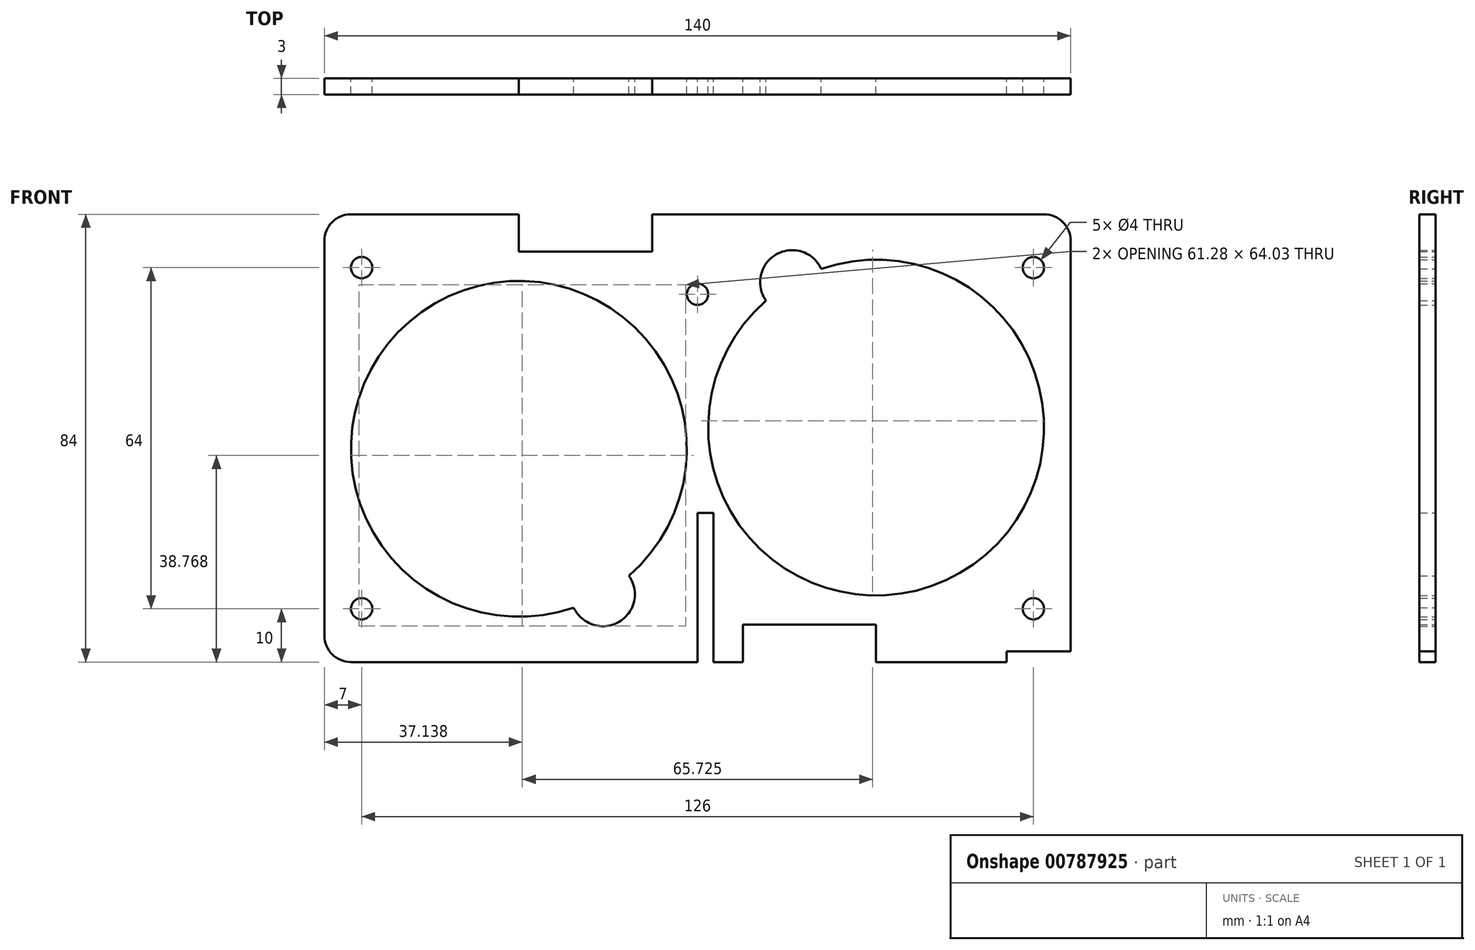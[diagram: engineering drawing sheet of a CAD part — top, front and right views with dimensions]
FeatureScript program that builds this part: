
annotation { "Feature Type Name" : "Feature", "Feature Type Description" : "" }
export const myFeature = defineFeature(function(context is Context, id is Id, definition is map)
    precondition{}
    {
        {
            var Q0;
            Q0=qCreatedBy(makeId("Front.planeOp"),FACE);
            var sketch = newSketch(context, id + "F0", { "sketchPlane" : qUnion([Q0])});
            skLineSegment(sketch, "E0.bottom", {"start": v(-65, -42) * mm, "end": v(0, -42) * mm});
            skLineSegment(sketch, "E0.top", {"start": v(-65, 42) * mm, "end": v(-33.5, 42) * mm});
            skLineSegment(sketch, "E0.left", {"start": v(-70, -37) * mm, "end": v(-70, 37) * mm});
            skLineSegment(sketch, "E0.right", {"start": v(70, -40) * mm, "end": v(70, 37) * mm});
            skPoint(sketch, "E0.middle", {"position": v(0, 0) * mm});
            skLineSegment(sketch, "E1", {"start": v(70, -40) * mm, "end": v(70, 2) * mm, "construction": true});
            skLineSegment(sketch, "E2", {"start": v(70, 2) * mm, "end": v(-70, 2) * mm, "construction": true});
            skLineSegment(sketch, "E3", {"start": v(-70, -42) * mm, "end": v(-70, -2) * mm, "construction": true});
            skLineSegment(sketch, "E4", {"start": v(-70, -2) * mm, "end": v(70, -2) * mm, "construction": true});
            skLineSegment(sketch, "E5", {"start": v(-70, -42) * mm, "end": v(0, -42) * mm, "construction": true});
            skLineSegment(sketch, "E6", {"start": v(0, -42) * mm, "end": v(0, 42) * mm, "construction": true});
            skLineSegment(sketch, "E7", {"start": v(0, -42) * mm, "end": v(0, 2) * mm, "construction": true});
            skLineSegment(sketch, "E8", {"start": v(0, -42) * mm, "end": v(0, -14) * mm});
            skLineSegment(sketch, "E9", {"start": v(0, -14) * mm, "end": v(0, -14) * mm});
            skLineSegment(sketch, "E10", {"start": v(-70, -42) * mm, "end": v(-33.5, -42) * mm, "construction": true});
            skLineSegment(sketch, "E11", {"start": v(-33.5, -42) * mm, "end": v(-33.5, 42) * mm, "construction": true});
            skPoint(sketch, "E12", {"position": v(-33.5, -2) * mm});
            skPoint(sketch, "E13", {"position": v(-33.5, 2) * mm});
            skArc(sketch, "E14", {"start": v(-12.86, -25.8) * mm, "mid": v(-49.25, 25.28) * mm, "end": v(-23.2, -31.77) * mm});
            skLineSegment(sketch, "E15", {"start": v(58, -42) * mm, "end": v(33.5, -42) * mm, "construction": true});
            skLineSegment(sketch, "E16", {"start": v(33.5, -42) * mm, "end": v(33.5, 42) * mm, "construction": true});
            skPoint(sketch, "E17", {"position": v(33.5, -2) * mm});
            skPoint(sketch, "E18", {"position": v(33.5, 2) * mm});
            skArc(sketch, "E19", {"start": v(12.86, 25.8) * mm, "mid": v(49.25, -25.28) * mm, "end": v(23.2, 31.77) * mm});
            skLineSegment(sketch, "E20", {"start": v(-33.5, -2) * mm, "end": v(-17.75, -29.28) * mm, "construction": true});
            skArc(sketch, "E21", {"start": v(-23.2, -31.77) * mm, "mid": v(-14.75, -34.48) * mm, "end": v(-12.86, -25.8) * mm});
            skLineSegment(sketch, "E22", {"start": v(-70, 42) * mm, "end": v(-63, 42) * mm, "construction": true});
            skLineSegment(sketch, "E23", {"start": v(-63, 42) * mm, "end": v(-63, -42) * mm, "construction": true});
            skLineSegment(sketch, "E24", {"start": v(-70, 42) * mm, "end": v(-70, 32) * mm, "construction": true});
            skLineSegment(sketch, "E25", {"start": v(-70, 32) * mm, "end": v(-63, 32) * mm, "construction": true});
            skLineSegment(sketch, "E26", {"start": v(-70, -42) * mm, "end": v(-70, -32) * mm, "construction": true});
            skLineSegment(sketch, "E27", {"start": v(-70, -32) * mm, "end": v(-63, -32) * mm, "construction": true});
            skCircle(sketch, "E28", {"center": v(-63, -32) * mm, "radius": 2 * mm});
            skLineSegment(sketch, "E29", {"start": v(70, 42) * mm, "end": v(63, 42) * mm, "construction": true});
            skLineSegment(sketch, "E30", {"start": v(63, 42) * mm, "end": v(63, -40) * mm, "construction": true});
            skLineSegment(sketch, "E31", {"start": v(70, 42) * mm, "end": v(70, 32) * mm, "construction": true});
            skLineSegment(sketch, "E32", {"start": v(70, 32) * mm, "end": v(63, 32) * mm, "construction": true});
            skLineSegment(sketch, "E33", {"start": v(70, -40) * mm, "end": v(70, -32) * mm, "construction": true});
            skLineSegment(sketch, "E34", {"start": v(70, -32) * mm, "end": v(63, -32) * mm, "construction": true});
            skCircle(sketch, "E35", {"center": v(63, 32) * mm, "radius": 2 * mm});
            skCircle(sketch, "E36", {"center": v(63, -32) * mm, "radius": 2 * mm});
            skPoint(sketch, "E37.visualSharp", {"position": v(-70, 42) * mm});
            skArc(sketch, "E37.filletArc", {"start": v(-65, 42) * mm, "mid": v(-68.54, 40.54) * mm, "end": v(-70, 37) * mm});
            skPoint(sketch, "E38.visualSharp", {"position": v(-70, -42) * mm});
            skArc(sketch, "E38.filletArc", {"start": v(-70, -37) * mm, "mid": v(-68.54, -40.54) * mm, "end": v(-65, -42) * mm});
            skPoint(sketch, "E39.visualSharp", {"position": v(70, 42) * mm});
            skArc(sketch, "E39.filletArc", {"start": v(70, 37) * mm, "mid": v(68.54, 40.54) * mm, "end": v(65, 42) * mm});
            skLineSegment(sketch, "E40", {"start": v(58, -42) * mm, "end": v(58, -40) * mm});
            skLineSegment(sketch, "E41", {"start": v(58, -40) * mm, "end": v(70, -40) * mm});
            skLineSegment(sketch, "E42.trimOffspring", {"start": v(3, -42) * mm, "end": v(8.5, -42) * mm});
            skLineSegment(sketch, "E43", {"start": v(0, -42) * mm, "end": v(0, 42) * mm});
            skPoint(sketch, "E44.orphan", {"position": v(70, -42) * mm});
            skLineSegment(sketch, "E45", {"start": v(33.5, -42) * mm, "end": v(33.5, -35) * mm});
            skLineSegment(sketch, "E46", {"start": v(33.5, -35) * mm, "end": v(8.5, -35) * mm});
            skLineSegment(sketch, "E47", {"start": v(8.5, -35) * mm, "end": v(8.5, -42) * mm});
            skLineSegment(sketch, "E48.trimOffspring", {"start": v(33.5, -42) * mm, "end": v(58, -42) * mm});
            skLineSegment(sketch, "E49", {"start": v(-8.5, 42) * mm, "end": v(-8.5, 35) * mm});
            skLineSegment(sketch, "E50", {"start": v(-8.5, 35) * mm, "end": v(-33.5, 35) * mm});
            skLineSegment(sketch, "E51", {"start": v(-33.5, 35) * mm, "end": v(-33.5, 42) * mm});
            skLineSegment(sketch, "E52.trimOffspring", {"start": v(-8.5, 42) * mm, "end": v(65, 42) * mm});
            skLineSegment(sketch, "E53", {"start": v(0, 42) * mm, "end": v(0, 27) * mm, "construction": true});
            skCircle(sketch, "E54", {"center": v(0, 27) * mm, "radius": 2 * mm});
            skLineSegment(sketch, "E55", {"start": v(33.5, 2) * mm, "end": v(17.75, 29.28) * mm, "construction": true});
            skArc(sketch, "E56", {"start": v(23.2, 31.77) * mm, "mid": v(14.75, 34.48) * mm, "end": v(12.86, 25.8) * mm});
            skLineSegment(sketch, "E57.trimOffspring", {"start": v(0, 27) * mm, "end": v(0, 42) * mm, "construction": true});
            skCircle(sketch, "E58", {"center": v(-63, 32) * mm, "radius": 2 * mm});
            skLineSegment(sketch, "E59", {"start": v(3, -14) * mm, "end": v(3, -42) * mm});
            skPoint(sketch, "E59.endSnap0", {"position": v(4.25, -42) * mm});
            skLineSegment(sketch, "E60", {"start": v(0, -14) * mm, "end": v(3, -14) * mm});
            skSolve(sketch);
        }
        {
            var Q0;
            Q0=makeQuery(id+"F0.imprint","IMPRINT",FACE,{"disambiguationData":[TD([[makeQuery(id+"F0.imprint","IMPRINT",EDGE,{"derivedFrom":sQuery(id+"F0.wireOp",EDGE,"E0.bottom")}),1.0]])]});
            var Q1;
            Q1=makeQuery(id+"F0.imprint","IMPRINT",FACE,{"disambiguationData":[TD([[makeQuery(id+"F0.imprint","IMPRINT",EDGE,{"derivedFrom":sQuery(id+"F0.wireOp",EDGE,"E0.right")}),1.0]])]});
            extrude(context, id + "F1", {"entities" : qUnion([Q0, Q1]), "depth" : 3 * mm, "offsetDistance" : 25 * mm});
        }
    });
